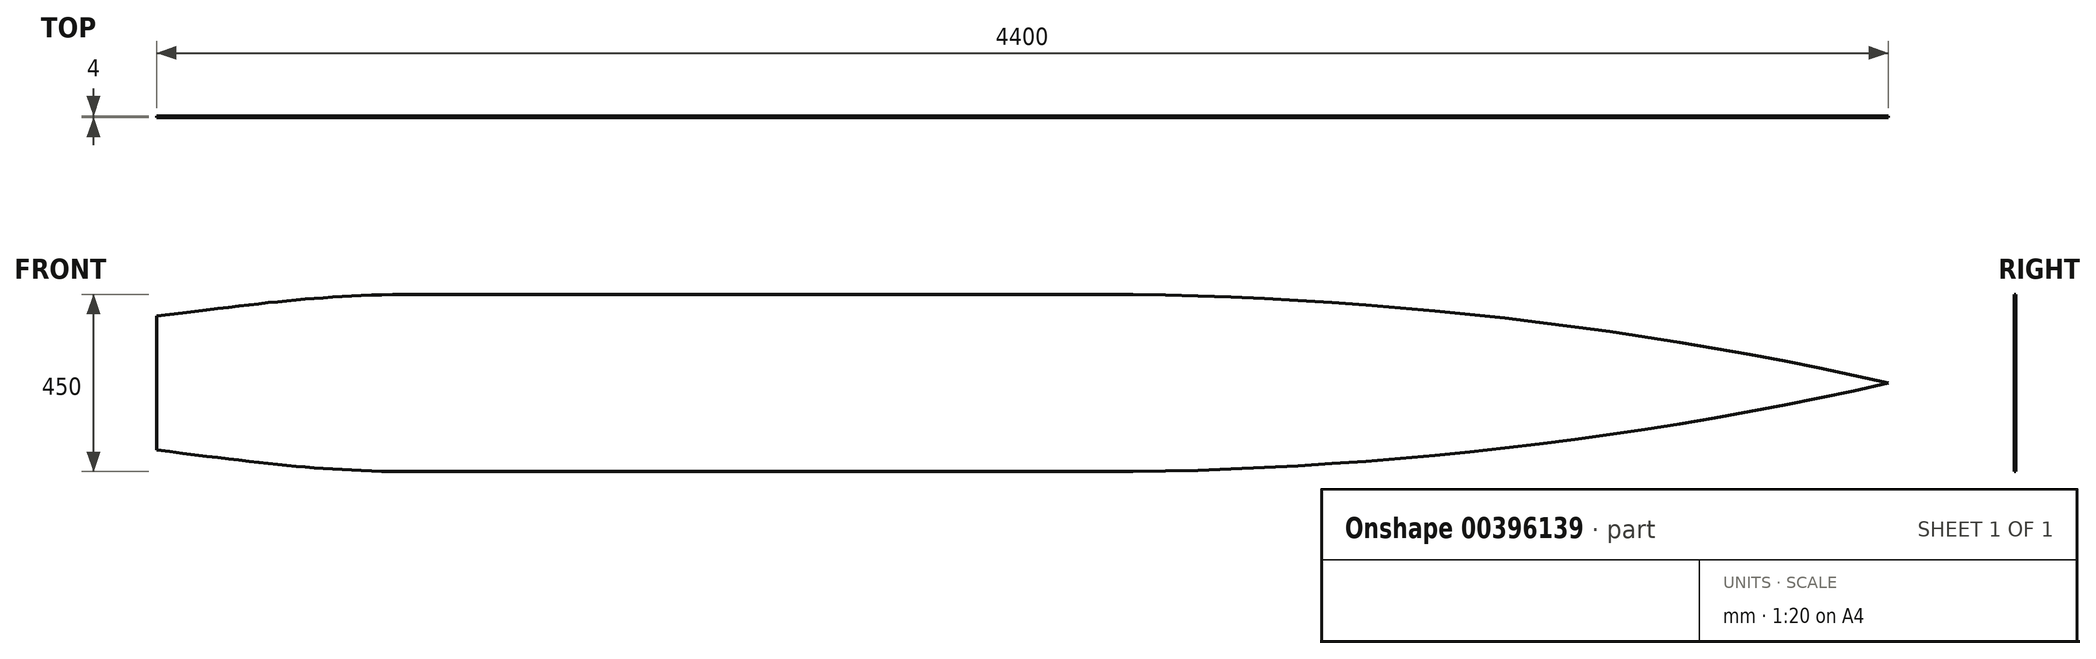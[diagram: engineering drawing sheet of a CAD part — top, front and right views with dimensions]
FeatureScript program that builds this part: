
annotation { "Feature Type Name" : "Feature", "Feature Type Description" : "" }
export const myFeature = defineFeature(function(context is Context, id is Id, definition is map)
    precondition{}
    {
        {
            var Q0;
            Q0=qCreatedBy(makeId("Front.planeOp"),FACE);
            var sketch = newSketch(context, id + "F0", { "sketchPlane" : qUnion([Q0])});
            skLineSegment(sketch, "E0.bottom", {"start": v(-1600, -225) * mm, "end": v(200, -225) * mm});
            skLineSegment(sketch, "E0.top", {"start": v(-1600, 225) * mm, "end": v(200, 225) * mm});
            skLineSegment(sketch, "E0.left", {"start": v(-2200, -170) * mm, "end": v(-2200, 170) * mm});
            skPoint(sketch, "E0.middle", {"position": v(0, 0) * mm});
            skLineSegment(sketch, "E1", {"start": v(0, 864.45) * mm, "end": v(0, -756.17) * mm, "construction": true});
            skLineSegment(sketch, "E2", {"start": v(-3455.42, 0) * mm, "end": v(3358.15, 0) * mm, "construction": true});
            skPoint(sketch, "E3", {"position": v(200, 225) * mm});
            skFitSpline(sketch, "E4", {"points": [v(200, 225) * mm, v(2200, 0) * mm, v(3932.85, -614.23) * mm], "startDerivative": vector(3613.88, 0) * mm, "endDerivative": vector(3088.29, -1525.8) * mm});
            skFitSpline(sketch, "E5.MirrorCS", {"points": [v(200, -225) * mm, v(2200, 0) * mm, v(3932.85, 614.23) * mm], "startDerivative": vector(3613.88, 0) * mm, "endDerivative": vector(3088.29, 1525.8) * mm});
            skPoint(sketch, "E6.orphan", {"position": v(2200, 225) * mm});
            skPoint(sketch, "E7.orphan", {"position": v(2200, -225) * mm});
            skPoint(sketch, "E8", {"position": v(-1600, 225) * mm});
            skPoint(sketch, "E9.MirrorP", {"position": v(-1600, -225) * mm});
            skPoint(sketch, "E10", {"position": v(-2200, 170) * mm});
            skPoint(sketch, "E11.MirrorP", {"position": v(-2200, -170) * mm});
            skFitSpline(sketch, "E12", {"points": [v(-1600, 225) * mm, v(-2200, 170) * mm, v(-3064.38, 0) * mm, v(-2200, -170) * mm, v(-1600, -225) * mm], "startDerivative": vector(-2845.7, -73.35) * mm, "endDerivative": vector(2845.7, -73.35) * mm});
            skPoint(sketch, "E13.orphan", {"position": v(-2200, 225) * mm});
            skPoint(sketch, "E14.orphan", {"position": v(-2200, -225) * mm});
            skLineSegment(sketch, "E15", {"start": v(200, 895.9) * mm, "end": v(200, -712.3) * mm, "construction": true});
            skSolve(sketch);
        }
        {
            var Q0;
            Q0=makeQuery(id+"F0.imprint","IMPRINT",FACE,{"disambiguationData":[TD([[makeQuery(id+"F0.imprint","IMPRINT",EDGE,{"derivedFrom":sQuery(id+"F0.wireOp",EDGE,"E0.bottom")}),1.0]])]});
            extrude(context, id + "F1", {"entities" : qUnion([Q0]), "depth" : 4 * mm});
        }
    });
